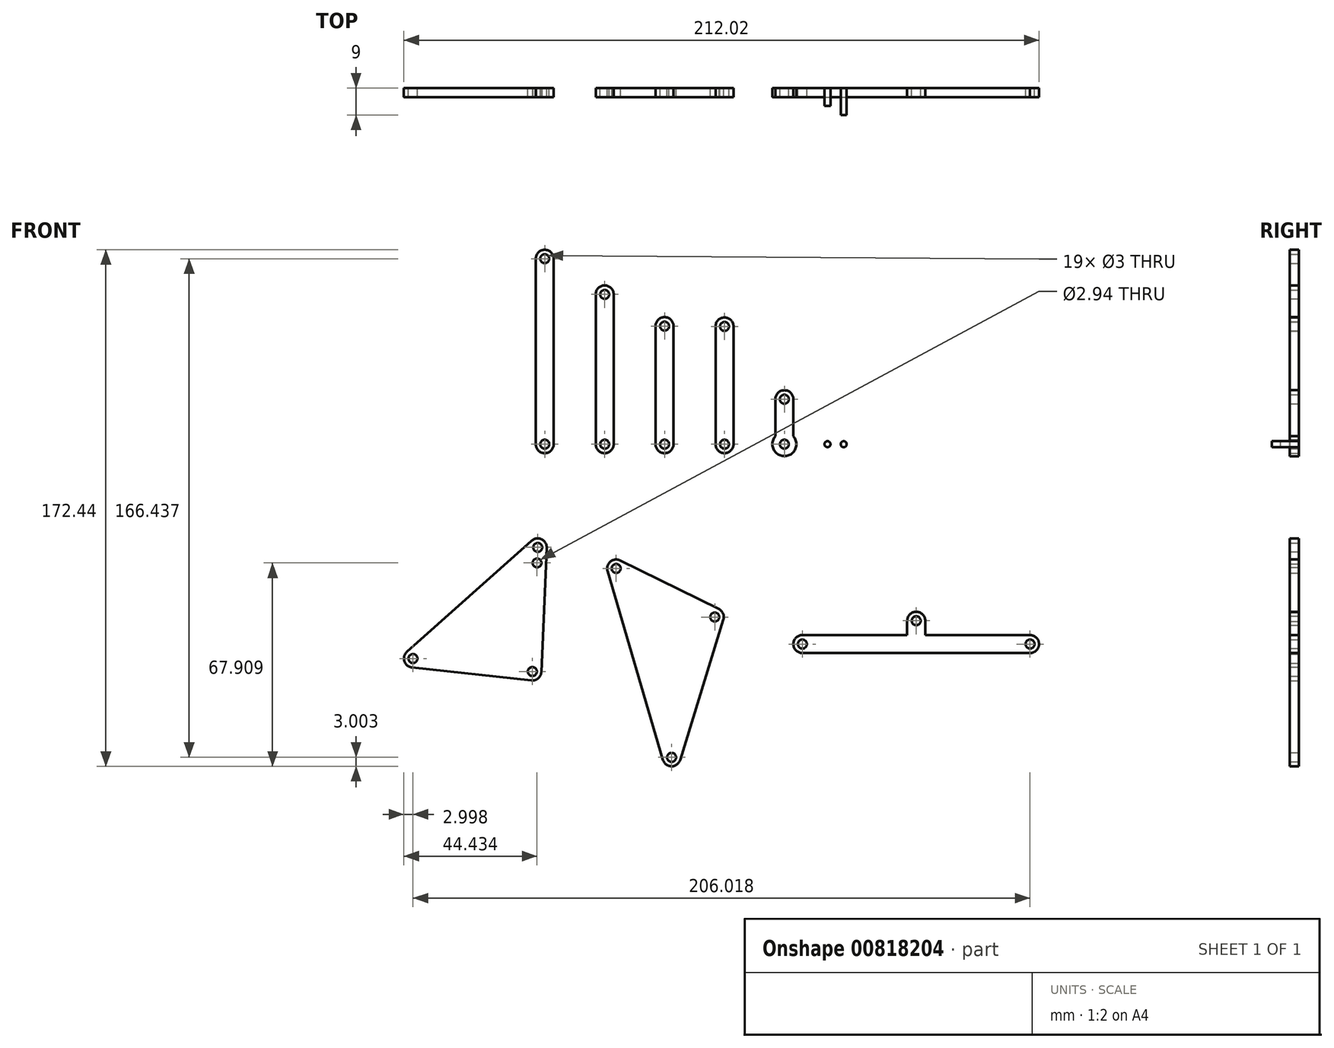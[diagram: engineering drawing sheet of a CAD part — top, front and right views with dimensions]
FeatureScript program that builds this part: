
annotation { "Feature Type Name" : "Feature", "Feature Type Description" : "" }
export const myFeature = defineFeature(function(context is Context, id is Id, definition is map)
    precondition{}
    {
        {
            var Q0;
            Q0=qCreatedBy(makeId("Front.planeOp"),FACE);
            var sketch = newSketch(context, id + "F0", { "sketchPlane" : qUnion([Q0])});
            skArc(sketch, "E0", {"start": v(-7, 15) * mm, "mid": v(-10, 18) * mm, "end": v(-13, 15) * mm});
            skLineSegment(sketch, "E1", {"start": v(-13, 15) * mm, "end": v(-13, 2.65) * mm});
            skLineSegment(sketch, "E2", {"start": v(-7, 15) * mm, "end": v(-7, 2.65) * mm});
            skCircle(sketch, "E3", {"center": v(-10, 15) * mm, "radius": 1.5 * mm});
            skCircle(sketch, "E4", {"center": v(-10, 0) * mm, "radius": 1.5 * mm});
            skArc(sketch, "E5", {"start": v(-33, 0) * mm, "mid": v(-30, -3) * mm, "end": v(-27, 0) * mm});
            skArc(sketch, "E6", {"start": v(-27, 39.3) * mm, "mid": v(-30, 42.3) * mm, "end": v(-33, 39.3) * mm});
            skLineSegment(sketch, "E7", {"start": v(-33, 39.3) * mm, "end": v(-33, 0) * mm});
            skLineSegment(sketch, "E8", {"start": v(-27, 39.3) * mm, "end": v(-27, 0) * mm});
            skCircle(sketch, "E9", {"center": v(-30, 39.3) * mm, "radius": 1.5 * mm});
            skCircle(sketch, "E10", {"center": v(-30, 0) * mm, "radius": 1.5 * mm});
            skArc(sketch, "E11", {"start": v(-53, 0) * mm, "mid": v(-50, -3) * mm, "end": v(-47, 0) * mm});
            skArc(sketch, "E12", {"start": v(-47, 39.4) * mm, "mid": v(-50, 42.4) * mm, "end": v(-53, 39.4) * mm});
            skLineSegment(sketch, "E13", {"start": v(-53, 39.4) * mm, "end": v(-53, 0) * mm});
            skLineSegment(sketch, "E14", {"start": v(-47, 39.4) * mm, "end": v(-47, 0) * mm});
            skCircle(sketch, "E15", {"center": v(-50, 39.4) * mm, "radius": 1.5 * mm});
            skCircle(sketch, "E16", {"center": v(-50, 0) * mm, "radius": 1.5 * mm});
            skArc(sketch, "E17", {"start": v(-73, 0) * mm, "mid": v(-70, -3) * mm, "end": v(-67, 0) * mm});
            skArc(sketch, "E18", {"start": v(-67, 50) * mm, "mid": v(-70, 53) * mm, "end": v(-73, 50) * mm});
            skLineSegment(sketch, "E19", {"start": v(-73, 50) * mm, "end": v(-73, 0) * mm});
            skLineSegment(sketch, "E20", {"start": v(-67, 50) * mm, "end": v(-67, 0) * mm});
            skCircle(sketch, "E21", {"center": v(-70, 50) * mm, "radius": 1.5 * mm});
            skCircle(sketch, "E22", {"center": v(-70, 0) * mm, "radius": 1.5 * mm});
            skArc(sketch, "E23", {"start": v(-93, 0) * mm, "mid": v(-90, -3) * mm, "end": v(-87, 0) * mm});
            skArc(sketch, "E24", {"start": v(-87, 61.9) * mm, "mid": v(-90, 64.9) * mm, "end": v(-93, 61.9) * mm});
            skLineSegment(sketch, "E25", {"start": v(-93, 61.9) * mm, "end": v(-93, 0) * mm});
            skLineSegment(sketch, "E26", {"start": v(-87, 61.9) * mm, "end": v(-87, 0) * mm});
            skCircle(sketch, "E27", {"center": v(-90, 61.9) * mm, "radius": 1.5 * mm});
            skCircle(sketch, "E28", {"center": v(-90, 0) * mm, "radius": 1.5 * mm});
            skLineSegment(sketch, "E29", {"start": v(-94.15, -75.92) * mm, "end": v(-92.35, -34.46) * mm, "construction": true});
            skLineSegment(sketch, "E30", {"start": v(-92.35, -34.46) * mm, "end": v(-134.01, -71.58) * mm, "construction": true});
            skLineSegment(sketch, "E31", {"start": v(-134.01, -71.58) * mm, "end": v(-94.15, -75.92) * mm, "construction": true});
            skLineSegment(sketch, "E32", {"start": v(-66.17, -41.5) * mm, "end": v(-33.24, -57.7) * mm, "construction": true});
            skPoint(sketch, "E32.startSnap0", {"position": v(-50, -3) * mm});
            skLineSegment(sketch, "E33", {"start": v(-33.24, -57.7) * mm, "end": v(-47.66, -104.54) * mm, "construction": true});
            skLineSegment(sketch, "E34", {"start": v(-47.66, -104.54) * mm, "end": v(-66.17, -41.5) * mm, "construction": true});
            skArc(sketch, "E35", {"start": v(-89.35, -34.58) * mm, "mid": v(-91.07, -31.74) * mm, "end": v(-94.35, -32.22) * mm});
            skArc(sketch, "E36", {"start": v(-94.47, -78.9) * mm, "mid": v(-92.2, -78.2) * mm, "end": v(-91.15, -76.05) * mm});
            skArc(sketch, "E37", {"start": v(-136, -69.34) * mm, "mid": v(-136.87, -72.5) * mm, "end": v(-134.34, -74.56) * mm});
            skLineSegment(sketch, "E38.0", {"start": v(-94.35, -32.22) * mm, "end": v(-136, -69.34) * mm});
            skLineSegment(sketch, "E39.0", {"start": v(-91.15, -76.05) * mm, "end": v(-89.35, -34.58) * mm});
            skLineSegment(sketch, "E40.0", {"start": v(-134.34, -74.56) * mm, "end": v(-94.47, -78.9) * mm});
            skCircle(sketch, "E41", {"center": v(-134.01, -71.58) * mm, "radius": 1.5 * mm});
            skCircle(sketch, "E42", {"center": v(-92.35, -34.46) * mm, "radius": 1.5 * mm});
            skCircle(sketch, "E43", {"center": v(-94.15, -75.92) * mm, "radius": 1.5 * mm});
            skArc(sketch, "E44", {"start": v(-64.84, -38.8) * mm, "mid": v(-68.1, -39.2) * mm, "end": v(-69.04, -42.34) * mm});
            skArc(sketch, "E45", {"start": v(-50.54, -105.38) * mm, "mid": v(-47.68, -107.54) * mm, "end": v(-44.8, -105.42) * mm});
            skArc(sketch, "E46", {"start": v(-30.37, -58.59) * mm, "mid": v(-30.49, -56.52) * mm, "end": v(-31.91, -55.02) * mm});
            skLineSegment(sketch, "E47.0", {"start": v(-50.54, -105.38) * mm, "end": v(-69.04, -42.34) * mm});
            skLineSegment(sketch, "E48.0", {"start": v(-64.84, -38.8) * mm, "end": v(-31.91, -55.02) * mm});
            skLineSegment(sketch, "E49.0", {"start": v(-30.37, -58.59) * mm, "end": v(-44.8, -105.42) * mm});
            skCircle(sketch, "E50", {"center": v(-66.17, -41.5) * mm, "radius": 1.5 * mm});
            skCircle(sketch, "E51", {"center": v(-33.24, -57.7) * mm, "radius": 1.5 * mm});
            skCircle(sketch, "E52", {"center": v(-47.66, -104.54) * mm, "radius": 1.5 * mm});
            skLineSegment(sketch, "E53", {"start": v(-4, -66.74) * mm, "end": v(34, -66.74) * mm, "construction": true});
            skLineSegment(sketch, "E54", {"start": v(34, -66.74) * mm, "end": v(72, -66.74) * mm, "construction": true});
            skLineSegment(sketch, "E55", {"start": v(34, -66.74) * mm, "end": v(34, -58.94) * mm, "construction": true});
            skArc(sketch, "E56", {"start": v(-4, -63.74) * mm, "mid": v(-7, -66.74) * mm, "end": v(-4, -69.74) * mm});
            skArc(sketch, "E57", {"start": v(72, -69.74) * mm, "mid": v(75, -66.7) * mm, "end": v(71.93, -63.74) * mm});
            skArc(sketch, "E58", {"start": v(37, -58.94) * mm, "mid": v(34, -55.94) * mm, "end": v(31, -58.94) * mm});
            skLineSegment(sketch, "E59", {"start": v(-4, -69.74) * mm, "end": v(72, -69.74) * mm});
            skLineSegment(sketch, "E60", {"start": v(-4, -63.74) * mm, "end": v(31, -63.74) * mm});
            skLineSegment(sketch, "E61", {"start": v(31, -58.94) * mm, "end": v(31, -63.74) * mm});
            skLineSegment(sketch, "E62", {"start": v(71.93, -63.74) * mm, "end": v(37, -63.74) * mm});
            skLineSegment(sketch, "E63", {"start": v(37, -58.94) * mm, "end": v(37, -63.74) * mm});
            skCircle(sketch, "E64", {"center": v(34, -58.94) * mm, "radius": 1.5 * mm});
            skCircle(sketch, "E65", {"center": v(72, -66.74) * mm, "radius": 1.5 * mm});
            skCircle(sketch, "E66", {"center": v(-4, -66.74) * mm, "radius": 1.5 * mm});
            skArc(sketch, "E67", {"start": v(-13, 2.65) * mm, "mid": v(-10, -4) * mm, "end": v(-7, 2.65) * mm});
            skCircle(sketch, "E68", {"center": v(-92.58, -39.63) * mm, "radius": 1.47 * mm});
            skSolve(sketch);
        }
        {
            assignVariable(context, id + "F1", {"name" : "thinkress", "anyValue" : 3});
        }
        {
            var Q0;
            Q0=makeQuery(id+"F0.imprint","IMPRINT",FACE,{"disambiguationData":[TD([[makeQuery(id+"F0.imprint","IMPRINT",EDGE,{"derivedFrom":sQuery(id+"F0.wireOp",EDGE,"E35")}),1.0]])]});
            var Q1;
            Q1=makeQuery(id+"F0.imprint","IMPRINT",FACE,{"disambiguationData":[TD([[makeQuery(id+"F0.imprint","IMPRINT",EDGE,{"derivedFrom":sQuery(id+"F0.wireOp",EDGE,"E44")}),1.0]])]});
            var Q2;
            Q2=makeQuery(id+"F0.imprint","IMPRINT",FACE,{"disambiguationData":[TD([[makeQuery(id+"F0.imprint","IMPRINT",EDGE,{"derivedFrom":sQuery(id+"F0.wireOp",EDGE,"E23")}),1.0]])]});
            var Q3;
            Q3=makeQuery(id+"F0.imprint","IMPRINT",FACE,{"disambiguationData":[TD([[makeQuery(id+"F0.imprint","IMPRINT",EDGE,{"derivedFrom":sQuery(id+"F0.wireOp",EDGE,"E17")}),1.0]])]});
            var Q4;
            Q4=makeQuery(id+"F0.imprint","IMPRINT",FACE,{"disambiguationData":[TD([[makeQuery(id+"F0.imprint","IMPRINT",EDGE,{"derivedFrom":sQuery(id+"F0.wireOp",EDGE,"E11")}),1.0]])]});
            var Q5;
            Q5=makeQuery(id+"F0.imprint","IMPRINT",FACE,{"disambiguationData":[TD([[makeQuery(id+"F0.imprint","IMPRINT",EDGE,{"derivedFrom":sQuery(id+"F0.wireOp",EDGE,"E5")}),1.0]])]});
            var Q6;
            Q6=makeQuery(id+"F0.imprint","IMPRINT",FACE,{"disambiguationData":[TD([[makeQuery(id+"F0.imprint","IMPRINT",EDGE,{"derivedFrom":sQuery(id+"F0.wireOp",EDGE,"EmJazmCR-fPvo-Zdi6-Hvz8-qesBlYHY8SAY")}),1.0]])]});
            var Q7;
            Q7=makeQuery(id+"F0.imprint","IMPRINT",FACE,{"disambiguationData":[TD([[makeQuery(id+"F0.imprint","IMPRINT",EDGE,{"derivedFrom":sQuery(id+"F0.wireOp",EDGE,"E56")}),1.0]])]});
            var Q8;
            Q8=makeQuery(id+"F0.imprint","IMPRINT",FACE,{"disambiguationData":[TD([[makeQuery(id+"F0.imprint","IMPRINT",EDGE,{"derivedFrom":sQuery(id+"F0.wireOp",EDGE,"E0")}),1.0]])]});
            extrude(context, id + "F2", {"entities" : qUnion([Q0, Q1, Q2, Q3, Q4, Q5, Q6, Q7, Q8]), "depth" : (getVariable(context, 'thinkress')) * mm, "offsetDistance" : 25 * mm});
        }
        {
            var Q0;
            Q0=qCreatedBy(makeId("Front.planeOp"),FACE);
            var sketch = newSketch(context, id + "F3", { "sketchPlane" : qUnion([Q0])});
            skCircle(sketch, "E69", {"center": v(4.4, 0) * mm, "radius": 1 * mm});
            skCircle(sketch, "E70", {"center": v(9.8, 0) * mm, "radius": 1 * mm});
            skSolve(sketch);
        }
        {
            var Q0;
            Q0=makeQuery(id+"F3.imprint","IMPRINT",FACE,{"disambiguationData":[TD([[makeQuery(id+"F3.imprint","IMPRINT",EDGE,{"derivedFrom":sQuery(id+"F3.wireOp",EDGE,"E69")}),1.0]])]});
            extrude(context, id + "F4", {"entities" : qUnion([Q0]), "depth" : (getVariable(context, 'thinkress') * 2) * mm, "offsetDistance" : 25 * mm});
        }
        {
            var Q0;
            Q0=makeQuery(id+"F3.imprint","IMPRINT",FACE,{"disambiguationData":[TD([[makeQuery(id+"F3.imprint","IMPRINT",EDGE,{"derivedFrom":sQuery(id+"F3.wireOp",EDGE,"E70")}),1.0]])]});
            extrude(context, id + "F5", {"entities" : qUnion([Q0]), "depth" : (getVariable(context, 'thinkress') * 3) * mm, "offsetDistance" : 25 * mm});
        }
    });
